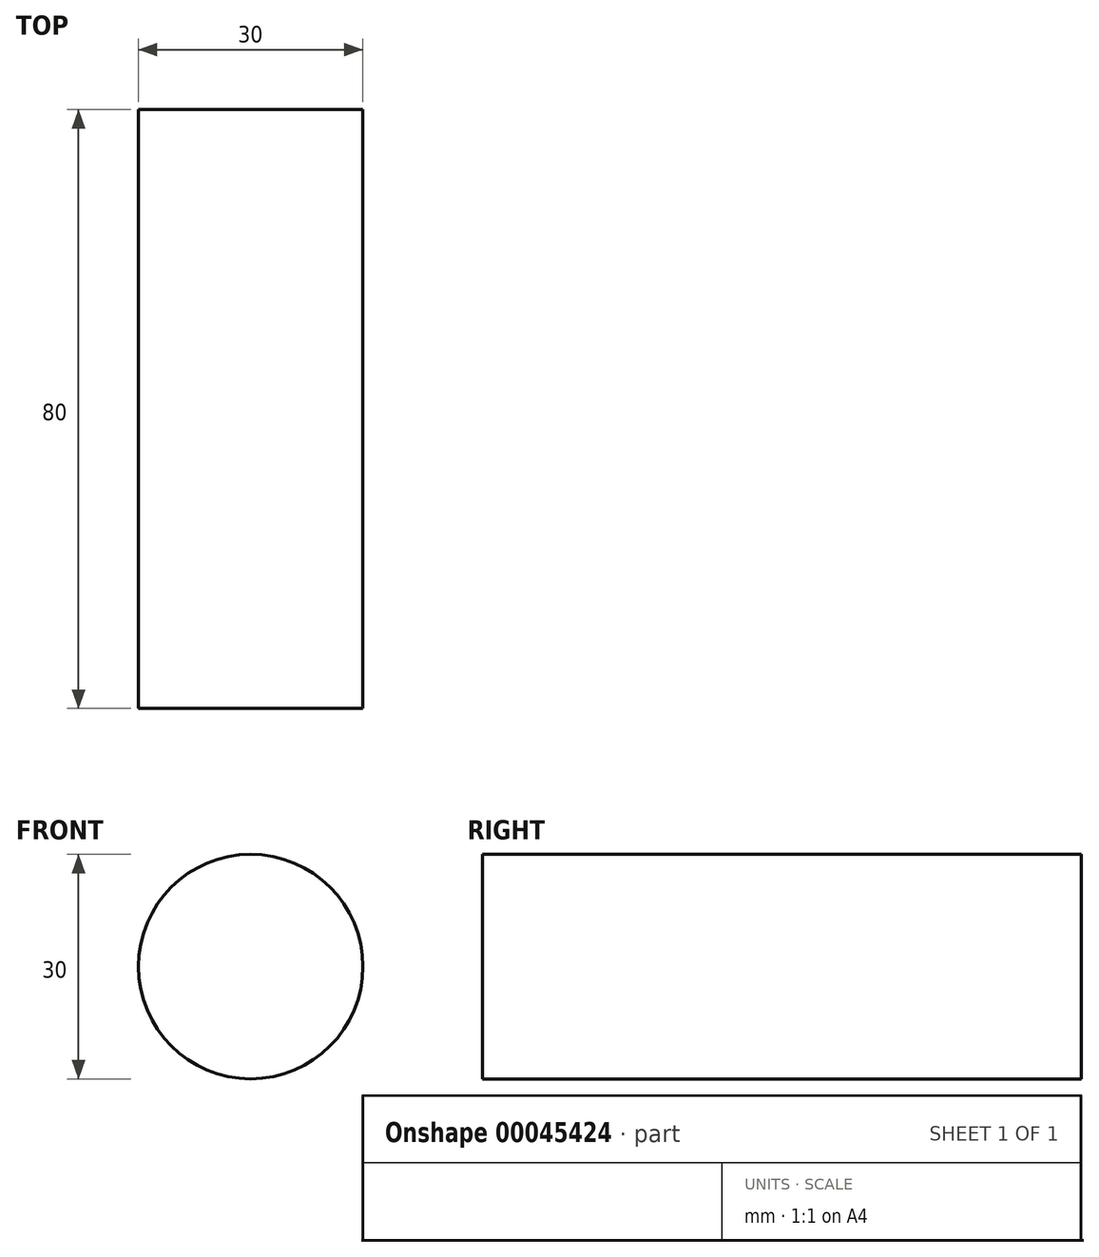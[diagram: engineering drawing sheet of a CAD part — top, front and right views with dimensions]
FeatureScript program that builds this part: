
annotation { "Feature Type Name" : "Feature", "Feature Type Description" : "" }
export const myFeature = defineFeature(function(context is Context, id is Id, definition is map)
    precondition{}
    {
        {
            var Q0;
            Q0=qCreatedBy(makeId("Front.planeOp"),FACE);
            var sketch = newSketch(context, id + "F0", { "sketchPlane" : qUnion([Q0])});
            skCircle(sketch, "E0", {"center": v(0, 0) * mm, "radius": 15 * mm});
            skSolve(sketch);
        }
        {
            var Q0;
            Q0=makeQuery(id+"F0.imprint","IMPRINT",FACE,{"disambiguationData":[TD([[makeQuery(id+"F0.imprint","IMPRINT",EDGE,{"derivedFrom":sQuery(id+"F0.wireOp",EDGE,"E0")}),1.0]])]});
            extrude(context, id + "F1", {"entities" : qUnion([Q0]), "oppositeDirection" : true, "depth" : 80 * mm});
        }
    });
